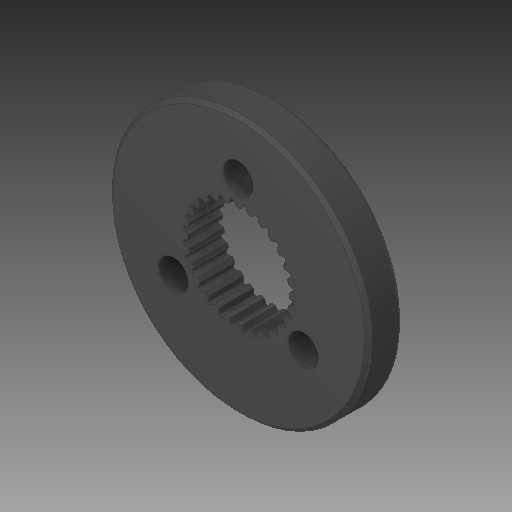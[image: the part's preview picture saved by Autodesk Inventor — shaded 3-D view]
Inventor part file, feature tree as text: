
AUTODESK INVENTOR PART (.ipt)
format: ipt  version: 2017 (Build 210142000, 142)  size: 276,480 bytes
history: native  units: in
note: dims shown in document units (in); Inventor stores cm internally (conversion verified against a paired STEP export)
features: chamfer x1
ambient origin geometry x8: Origin, YZ Plane, XZ Plane, XY Plane, X Axis, Y Axis, Z Axis, Center Point
bodies: Solid1 (feature_tree)
feature tree (1):
  chamfer  "Chamfer1"  [1 undecoded]
note: 1 required parameter value undecoded (feature->parameter linkage not recoverable at this tier; creation-order binding heuristic only, values carry confidence <= 0.55)
